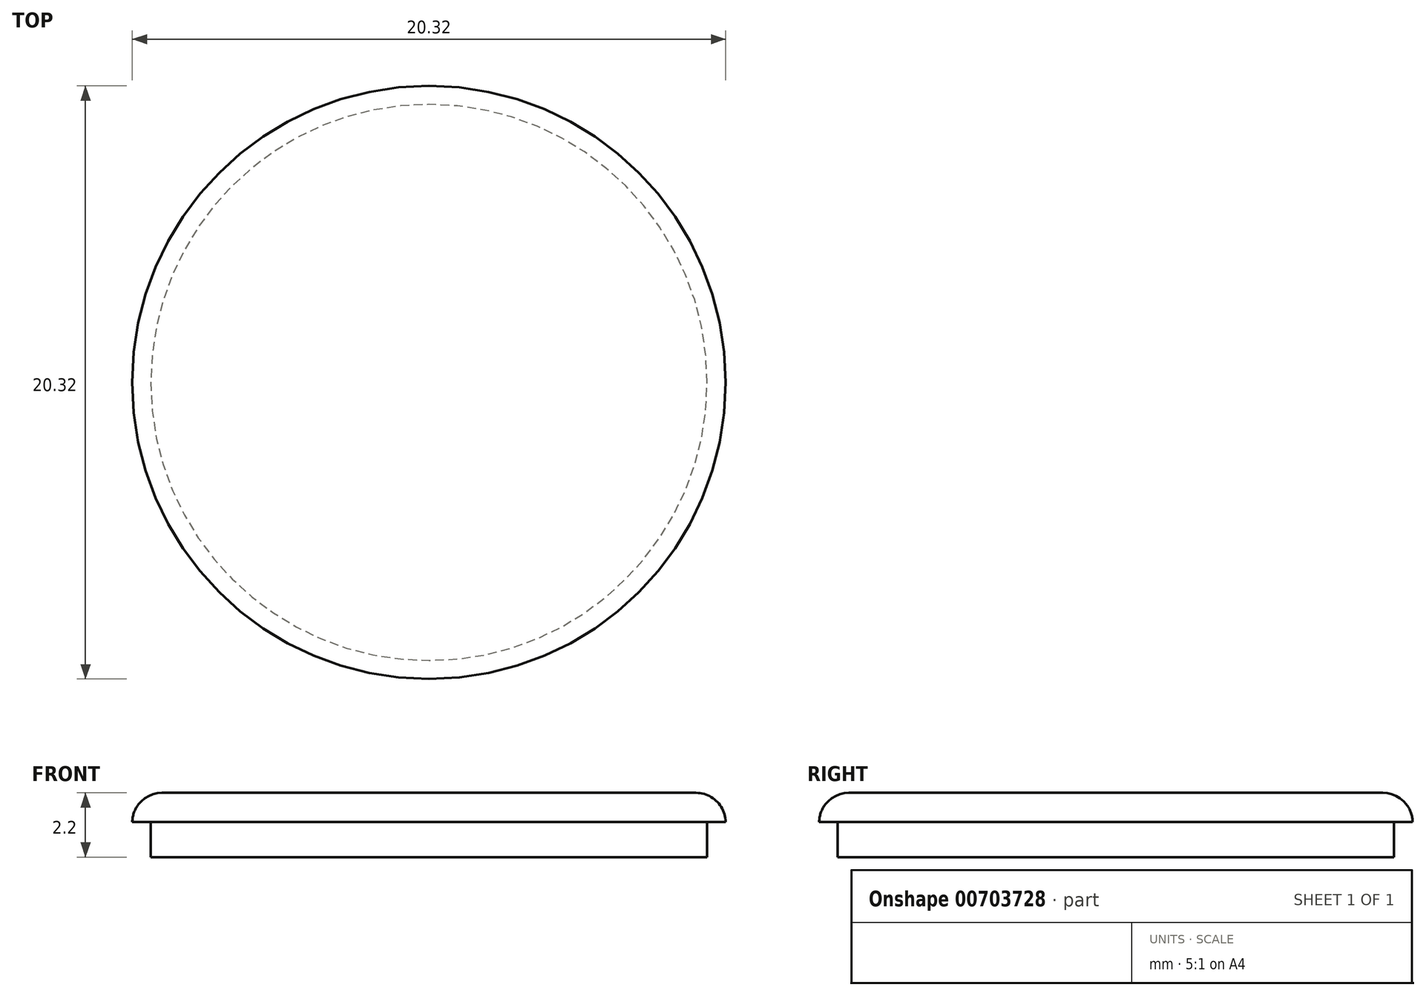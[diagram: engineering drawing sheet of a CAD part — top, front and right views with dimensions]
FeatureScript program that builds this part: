
annotation { "Feature Type Name" : "Feature", "Feature Type Description" : "" }
export const myFeature = defineFeature(function(context is Context, id is Id, definition is map)
    precondition{}
    {
        {
            var Q0;
            Q0=qCreatedBy(makeId("Front.planeOp"),FACE);
            var sketch = newSketch(context, id + "F0", { "sketchPlane" : qUnion([Q0])});
            skLineSegment(sketch, "E0", {"start": v(0, 0) * mm, "end": v(-9.53, 0) * mm});
            skLineSegment(sketch, "E1", {"start": v(-9.53, 0) * mm, "end": v(-9.53, 1.2) * mm});
            skLineSegment(sketch, "E2", {"start": v(-9.53, 1.2) * mm, "end": v(-10.16, 1.2) * mm});
            skLineSegment(sketch, "E3", {"start": v(-10.16, 1.2) * mm, "end": v(-10.16, 2.2) * mm});
            skLineSegment(sketch, "E4", {"start": v(-10.16, 2.2) * mm, "end": v(0, 2.2) * mm});
            skLineSegment(sketch, "E5", {"start": v(0, 2.2) * mm, "end": v(0, 0) * mm});
            skSolve(sketch);
        }
        {
            var Q0;
            Q0=makeQuery(id+"F0.imprint","IMPRINT",FACE,{"disambiguationData":[TD([[makeQuery(id+"F0.imprint","IMPRINT",EDGE,{"derivedFrom":sQuery(id+"F0.wireOp",EDGE,"E0")}),-1.0]])]});
            var Q1;
            Q1=sQuery(id+"F0.wireOp",EDGE,"E5");
            revolve(context, id + "F1", {"surfaceOperationType" : NewSurfaceOperationType.NEW, "entities" : qUnion([Q0]), "axis" : qUnion([Q1]), "revolveType" : RevolveType.FULL});
        }
        {
            var Q0;
            Q0=makeQuery(id+"F1.opRevolve","SWEPT_EDGE",EDGE,{"disambiguationData":[OSD([sQuery(id+"F0.wireOp",EDGE,"E3"),sQuery(id+"F0.wireOp",EDGE,"E4")])]});
            fillet(context, id + "F2", {"entities" : qUnion([Q0]), "radius" : 1.02 * mm, "tangentPropagation" : true, "allowEdgeOverflow" : false});
        }
    });
